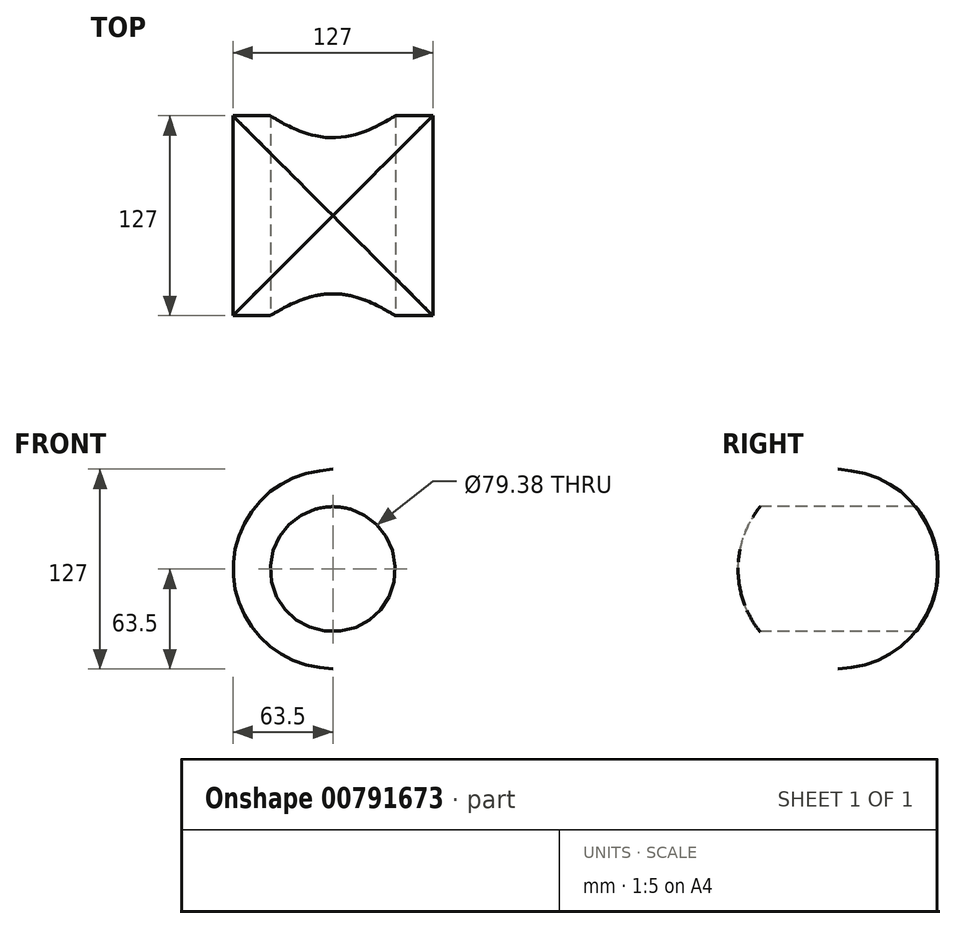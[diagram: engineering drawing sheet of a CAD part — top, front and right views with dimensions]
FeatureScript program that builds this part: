
annotation { "Feature Type Name" : "Feature", "Feature Type Description" : "" }
export const myFeature = defineFeature(function(context is Context, id is Id, definition is map)
    precondition{}
    {
        {
            var Q0;
            Q0=qCreatedBy(makeId("Front.planeOp"),FACE);
            var sketch = newSketch(context, id + "F0", { "sketchPlane" : qUnion([Q0])});
            skPoint(sketch, "E0.middle", {"position": v(0, 0) * mm});
            skCircle(sketch, "E1", {"center": v(0, 0) * mm, "radius": 38.1 * mm});
            skCircle(sketch, "E2.0", {"center": v(0, 0) * mm, "radius": 39.69 * mm});
            skCircle(sketch, "E3", {"center": v(0, 0) * mm, "radius": 63.5 * mm});
            skSolve(sketch);
        }
        {
            var Q0;
            Q0=qCreatedBy(makeId("Right.planeOp"),FACE);
            var sketch = newSketch(context, id + "F1", { "sketchPlane" : qUnion([Q0])});
            skCircle(sketch, "E4", {"center": v(0, 0) * mm, "radius": 25.4 * mm});
            skCircle(sketch, "E5.0", {"center": v(0, 0) * mm, "radius": 26.99 * mm});
            skCircle(sketch, "E6", {"center": v(0, 0) * mm, "radius": 63.5 * mm});
            skCircle(sketch, "E7", {"center": v(0, 0) * mm, "radius": 76.2 * mm});
            skSolve(sketch);
        }
        {
            var Q0;
            Q0=makeQuery(id+"F0.imprint","IMPRINT",FACE,{"disambiguationData":[TD([[makeQuery(id+"F0.imprint","IMPRINT",EDGE,{"derivedFrom":sQuery(id+"F0.wireOp",EDGE,"E1")}),-1.0]])]});
            extrude(context, id + "F2", {"entities" : qUnion([Q0]), "oppositeDirection" : true, "depth" : 50.8 * mm, "offsetDistance" : 25.4 * mm, "hasSecondDirection" : true, "secondDirectionOppositeDirection" : false, "secondDirectionDepth" : 50.8 * mm});
        }
        {
            var Q0;
            Q0=makeQuery(id+"F1.imprint","IMPRINT",FACE,{"disambiguationData":[TD([[makeQuery(id+"F1.imprint","IMPRINT",EDGE,{"derivedFrom":sQuery(id+"F1.wireOp",EDGE,"E4")}),-1.0]])]});
            var Q1;
            Q1=makeQuery(id+"F1.imprint","IMPRINT",FACE,{"disambiguationData":[TD([[makeQuery(id+"F1.imprint","IMPRINT",EDGE,{"derivedFrom":sQuery(id+"F1.wireOp",EDGE,"E4")}),1.0]])]});
            var Q2;
            Q2=makeQuery(id+"F1.imprint","IMPRINT",FACE,{"disambiguationData":[TD([[makeQuery(id+"F1.imprint","IMPRINT",EDGE,{"derivedFrom":sQuery(id+"F1.wireOp",EDGE,"E5.0")}),-1.0]])]});
            extrude(context, id + "F3", {"entities" : qUnion([Q0, Q1, Q2]), "depth" : 63.5 * mm, "offsetDistance" : 25.4 * mm, "hasSecondDirection" : true, "secondDirectionOppositeDirection" : true, "secondDirectionDepth" : 63.5 * mm});
        }
        {
            var Q0;
            Q0=qCreatedBy(makeId("Right.planeOp"),FACE);
            var sketch = newSketch(context, id + "F4", { "sketchPlane" : qUnion([Q0])});
            skCircle(sketch, "E8", {"center": v(0, 0) * mm, "radius": 6.35 * mm});
            skSolve(sketch);
        }
        {
            var Q0;
            Q0=makeQuery(id+"F4.imprint","IMPRINT",FACE,{"disambiguationData":[TD([[makeQuery(id+"F4.imprint","IMPRINT",EDGE,{"derivedFrom":sQuery(id+"F4.wireOp",EDGE,"E8")}),1.0]])]});
            extrude(context, id + "F5", {"entities" : qUnion([Q0]), "operationType" : NewBodyOperationType.ADD, "endBound" : BoundingType.SYMMETRIC, "depth" : 101.6 * mm, "offsetDistance" : 25.4 * mm});
        }
        {
            var Q0;
            Q0=makeQuery(id+"F0.imprint","IMPRINT",FACE,{"disambiguationData":[TD([[makeQuery(id+"F0.imprint","IMPRINT",EDGE,{"derivedFrom":sQuery(id+"F0.wireOp",EDGE,"E2.0")}),-1.0]])]});
            extrude(context, id + "F6", {"entities" : qUnion([Q0]), "operationType" : NewBodyOperationType.INTERSECT, "endBound" : BoundingType.SYMMETRIC, "oppositeDirection" : true, "depth" : 127 * mm, "offsetDistance" : 25.4 * mm});
        }
    });
